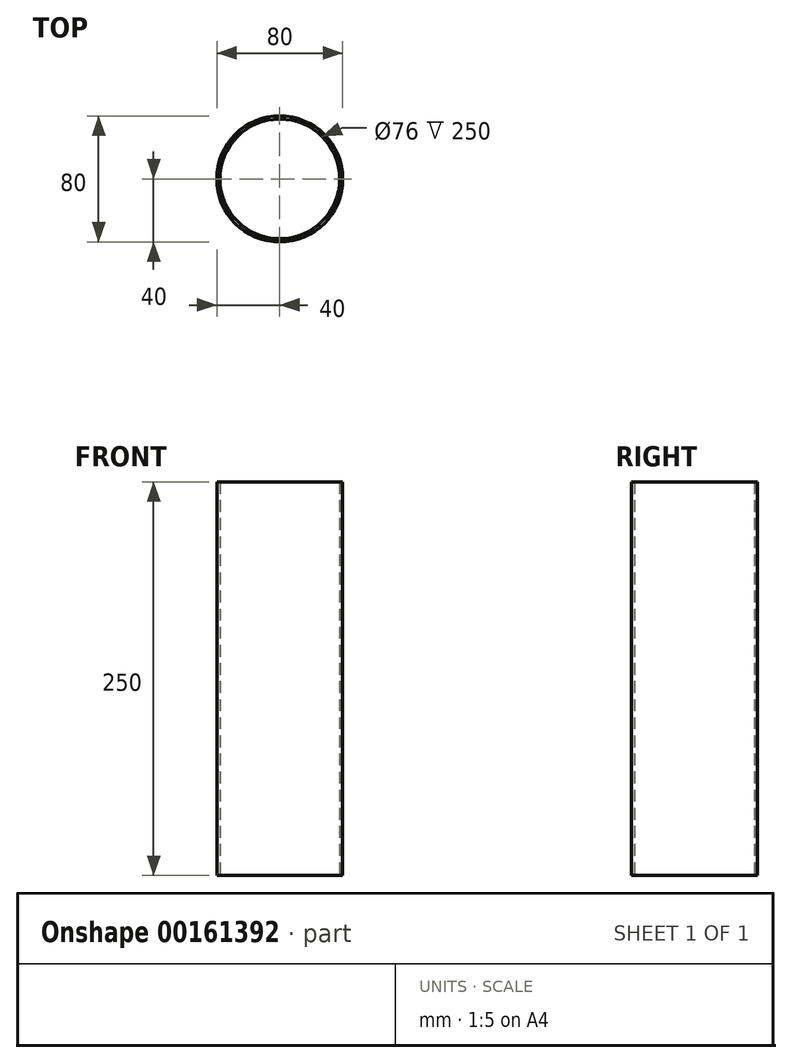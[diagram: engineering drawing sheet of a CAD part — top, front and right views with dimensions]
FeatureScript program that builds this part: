
annotation { "Feature Type Name" : "Feature", "Feature Type Description" : "" }
export const myFeature = defineFeature(function(context is Context, id is Id, definition is map)
    precondition{}
    {
        {
            var Q0;
            Q0=qCreatedBy(makeId("Top.planeOp"),FACE);
            var sketch = newSketch(context, id + "F0", { "sketchPlane" : qUnion([Q0])});
            skCircle(sketch, "E0", {"center": v(0, 0) * mm, "radius": 40 * mm});
            skCircle(sketch, "E1.0", {"center": v(0, 0) * mm, "radius": 38 * mm});
            skSolve(sketch);
        }
        {
            var Q0;
            Q0=makeQuery(id+"F0.imprint","IMPRINT",FACE,{"disambiguationData":[TD([[makeQuery(id+"F0.imprint","IMPRINT",EDGE,{"derivedFrom":sQuery(id+"F0.wireOp",EDGE,"E0")}),1.0]])]});
            extrude(context, id + "F1", {"entities" : qUnion([Q0]), "depth" : 250 * mm});
        }
    });
